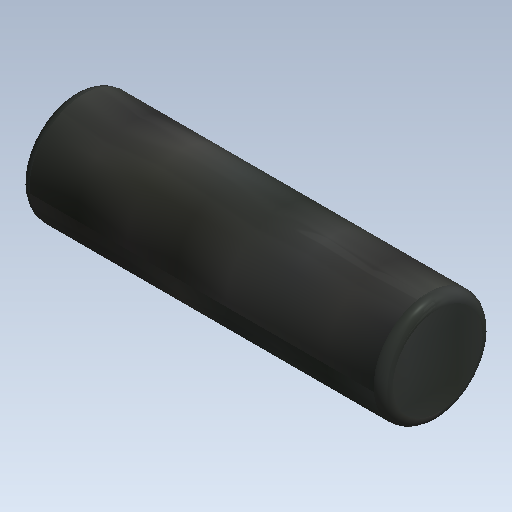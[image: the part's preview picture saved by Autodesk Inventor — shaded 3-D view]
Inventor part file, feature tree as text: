
AUTODESK INVENTOR PART (.ipt)
format: ipt  version: 2021 (Build 250183000, 183)  size: 118,784 bytes
history: native  units: mm (DEFAULTED — no unit token found)
features: other x7, revolve x1, sketch x1
ambient origin geometry x8: Origin, YZ Plane, XZ Plane, XY Plane, X Axis, Y Axis, Z Axis, Center Point
bodies: Solid1 (feature_tree)
feature tree (9):
  revolve  "Revolution1"  [1 undecoded]
  other  "IP_1_XY"
  other  "IP_1_YZ"
  other  "IP_1_ZX"
  other  "IP_1_X"
  other  "IP_1_Y"
  other  "IP_1_Z"
  other  "IP_1_Center"
  sketch  "Sketch_1"  dims[d0=360.0deg]
note: 1 required parameter value undecoded (feature->parameter linkage not recoverable at this tier; creation-order binding heuristic only, values carry confidence <= 0.55)
